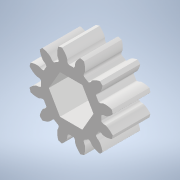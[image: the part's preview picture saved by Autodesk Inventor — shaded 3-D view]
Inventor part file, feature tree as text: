
AUTODESK INVENTOR PART (.ipt)
format: ipt  version: 2022 (Build 260153000, 153)  size: 2,653,184 bytes
history: native  units: mm
features: sketch x2, extrude x2
ambient origin geometry x8: Origin, YZ Plane, XZ Plane, XY Plane, X Axis, Y Axis, Z Axis, Center Point
bodies: Solid1 (feature_tree)
feature tree (4):
  sketch  "Sketch1"  dims[d10=6.2mm d11=0.0mm d30=3.1mm]
  extrude  "Extrusion1"  Depth=6.2mm
  extrude  "Extrusion8"  Depth=10.0mm
  sketch  "Sketch4"  dims[d31=60.0mm d33=360.0deg d37=0.5mm d38=10.0mm d39=0.0mm]
